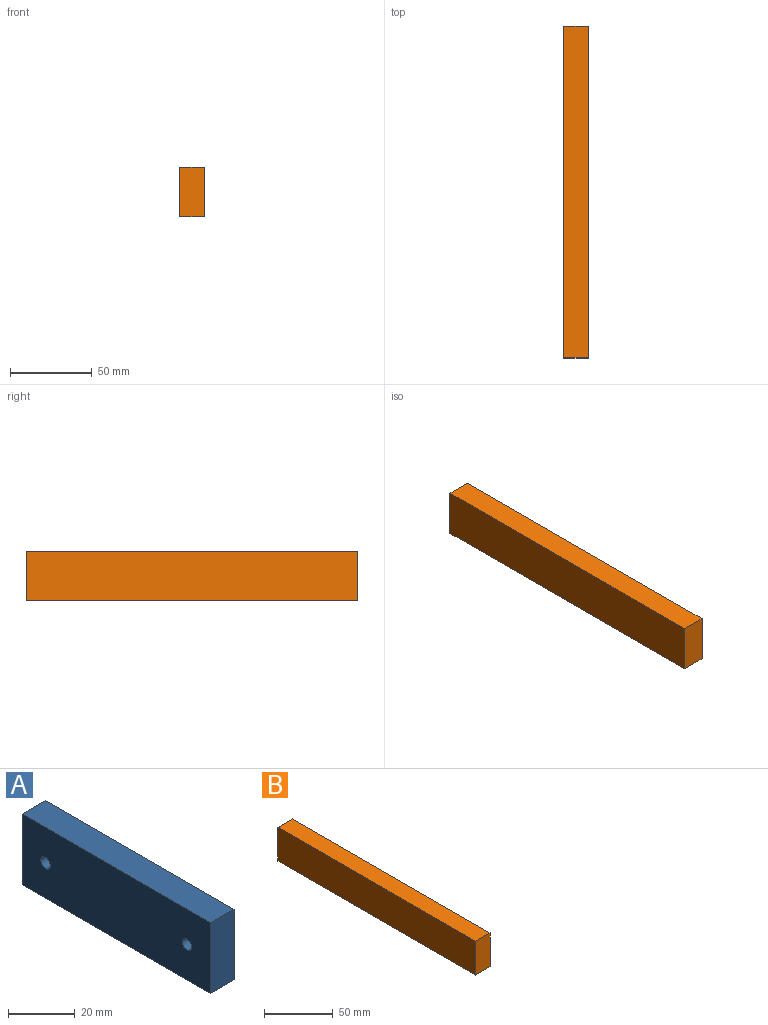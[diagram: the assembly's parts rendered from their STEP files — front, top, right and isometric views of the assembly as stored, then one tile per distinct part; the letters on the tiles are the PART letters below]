
ASSEMBLY  parts=2 mates=1
PART A: 8 faces, bbox 10x80x26 mm
  f0: plane 80x26mm, normal (1,0,0), area 2054.9mm2, adj f1,f3,f4,f5,f6,f7
  f1: plane 80x10mm, normal (0,0,1), area 800mm2, adj f0,f2,f4,f5
  f2: plane 80x26mm, normal (-1,0,0), area 2054.9mm2, adj f1,f3,f4,f5,f6,f7
  f3: plane 80x10mm, normal (0,0,-1), area 800mm2, adj f0,f2,f4,f5
  f4: plane 26x10mm, normal (0,-1,0), area 260mm2, adj f0,f1,f2,f3
  f5: plane 26x10mm, normal (0,1,0), area 260mm2, adj f0,f1,f2,f3
  f6: cylinder r=2mm len=10mm, axis (-1,0,0), area 125.7mm2, adj f0,f2
  f7: cylinder r=2mm len=10mm, axis (-1,0,0), area 125.7mm2, adj f0,f2
PART B: 18 faces, bbox 15x203x30 mm
  f0: plane 6.5x1.5mm, normal (0,1,0), area 9.8mm2, adj f1,f2,f13,f15
  f1: plane 200x10mm, normal (-1,0,0), area 1350mm2, adj f0,f4,f10,f13,f15,f16
  f2: plane 203x30mm, normal (1,0,0), area 3390mm2, adj f0,f7,f8,f10,f11,f12,f13,f14
  f3: plane 200x27mm, normal (1,0,0), area 5400mm2, adj f4,f9,f10,f16
  f4: plane 200x12mm, normal (0,0,-1), area 2400mm2, adj f1,f3,f10,f16
  f5: plane 200x10mm, normal (-1,0,0), area 1350mm2, adj f9,f10,f11,f12,f14,f16
  f6: plane 203x30mm, normal (-1,0,0), area 6090mm2, adj f7,f8,f10,f17
  f7: plane 203x15mm, normal (0,0,-1), area 3045mm2, adj f2,f6,f10,f17
  f8: plane 203x15mm, normal (0,0,1), area 3045mm2, adj f2,f6,f10,f17
  f9: plane 200x12mm, normal (0,0,1), area 2400mm2, adj f3,f5,f10,f16
  f10: plane 30x15mm, normal (0,1,0), area 96mm2, adj f1,f2,f3,f4,f5,f6,f7,f8
  f11: plane 6.5x1.5mm, normal (0,1,0), area 9.7mm2, adj f2,f5,f12,f14
  f12: plane 100x1.5mm, normal (0,0,1), area 150mm2, adj f2,f5,f10,f11
  f13: plane 100x1.5mm, normal (0,0,-1), area 150mm2, adj f0,f1,f2,f10
  f14: plane 100x1.5mm, normal (0,0,1), area 150mm2, adj f2,f5,f11,f16
  f15: plane 100x1.5mm, normal (0,0,-1), area 150mm2, adj f0,f1,f2,f16
  f16: plane 27x13.5mm, normal (0,1,0), area 334.5mm2, adj f1,f2,f3,f4,f5,f9,f14,f15
  f17: plane 30x15mm, normal (0,-1,0), area 450mm2, adj f2,f6,f7,f8
PLACE A t=(-21.83,93.73,-28.14)mm
PLACE B t=(-83.72,153.73,-30.14)mm
MATE fastened A.f2 <-> B.f3  axis (-1,0,0) through (-82.22,53.73,-15.14)mm
